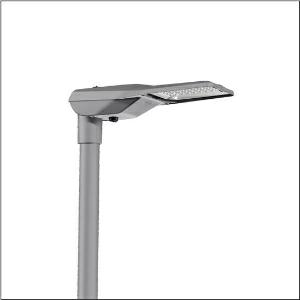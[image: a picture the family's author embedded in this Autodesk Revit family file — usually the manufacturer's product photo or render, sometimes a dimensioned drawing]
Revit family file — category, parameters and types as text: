
# Revit family: streetlight_sl_21_iq_mini___st1_0a_5xe2d21y08jb_5dbb
name_source: partatom
category: Lighting Fixtures
units: mm (PartAtom-declared; Revit-internal decimal feet)

## family parameters
Cut with Voids When Loaded = No
Host = Face
Light Source = No
Part Type = Normal
Room Calculation Point = No
Round Connector Dimension = Use Diameter
Shared = No

## types (1)
- --- (1 x LED, 9000 lm, 72.5 W, 2200K)
    Apparent Load = 73 VA
    CIE Flux Codes = 40 73 97 100 100
    Color Rendering = 70
    Color Temperature = 2200K
    Default Elevation = 1800 mm
    Description = Streetlight SL 21 iQ mini, mast luminaire, primary light control with lens, of PMMA, primary optical cover: cover, of toughened safety glass, transparent, light distribution: ST1.0a, light emission: direct distribution, primary light characteristic: asymmetric, installation type: post-top, side-entry, LED, High Power LED, rated luminous flux: 9.000lm, luminous efficacy: 124lm/W, light colour: 722, colour temperature: 2200K, control: pre-setting: logarithmic dimming characteristic, Street-Remote, Auto-Match, Temp-Guard, Lumen-Switch, Night-Set, Smart-Wire, Light-Fading, Desk-Remote (wireless, voltage-free reading and setting of iQ features in the workshop via application-optimized NFC function/RFID function), optimised constant luminous flux control (CLO 2.0), mains connection: 220..240V, AC, 50/60Hz, start of lifetime: 73W, end of service life: 76W, reduction: 33W, luminaire housing, of diecast aluminium, powder-coated, Siteco® metallic grey (DB 702S), corrosivity category C5 mid according to DIN EN ISO 12944, please order mast flange separately, inclination adjustable: 0°, 5°, 10°, 15°, sealing non-destructively replaceable, multi-level sealing system, length: 628mm, width: 235mm, height: 110mm, mast flange for spigot size: 42mm (side-entry): 5XC10008XM4, 60/48mm (side-entry/post-top): 5XC10108XM2, 76/60mm (side-entry/post-top): 5XC10108XM1, Smart Interface below and above, protection rating (complete): IP66, insulation class (complete): insulation class II (safety insulation), certification: CE, ENEC, ENEC+, VDE, impact resistance: IK09, permissible operating ambient temperature for outdoor applications: -40..+50°C, standard-compliant lighting for roads and squares, packaging unit: 1 piece

Light Distribution: ST1.0a
    Height = 110 mm
    Lamp = 1 x LED
    Lamp Light Flux = 9000 lm
    Lamp Power = 72.5 W
    Lamp count = 1
    Length = 625 mm
    Luminous efficacy = 124 lm/W
    Manufacturer = Siteco
    ModVariant = No
    Model = 5XE2D21Y08JB
    Number of Poles = 1
    OnlyDefault = Yes
    Power Factor = 1
    Product Name = Streetlight SL 21 iQ mini | ST1.0a
    Product group = mast luminaire | pylon top
    ProductGroupID = 6100
    Protection Class = Protection class II
    Protection Degree = IP 66
    RLX_Detail_Level = 1
    RLX_Emergency_Light_Flux = 0 lm
    RLX_Emergency_Type = 0
    RLX_Emergency_Type_DB = No
    RlxData = <blob elided: 92125 chars, md5=58a8d3f6>
    Socket = socket
    Standby Power = 0 W
    System Light Flux = 9000 lm
    System Power = 73 W
    Type Comments = factory setting: luminous flux: 100 % | dim-lin: 254 | 755 mA
    Type Image = l_1003514.jpg
    URL = http://relux.com
    VarID = @adj_082995
    Voltage = 0 V
    Weight = 0.00 kg
    Width = 234 mm

## geometry (parser evidence)
native form markers: Blend x4, Sweep x9
no freeform markers — native parametric forms only
